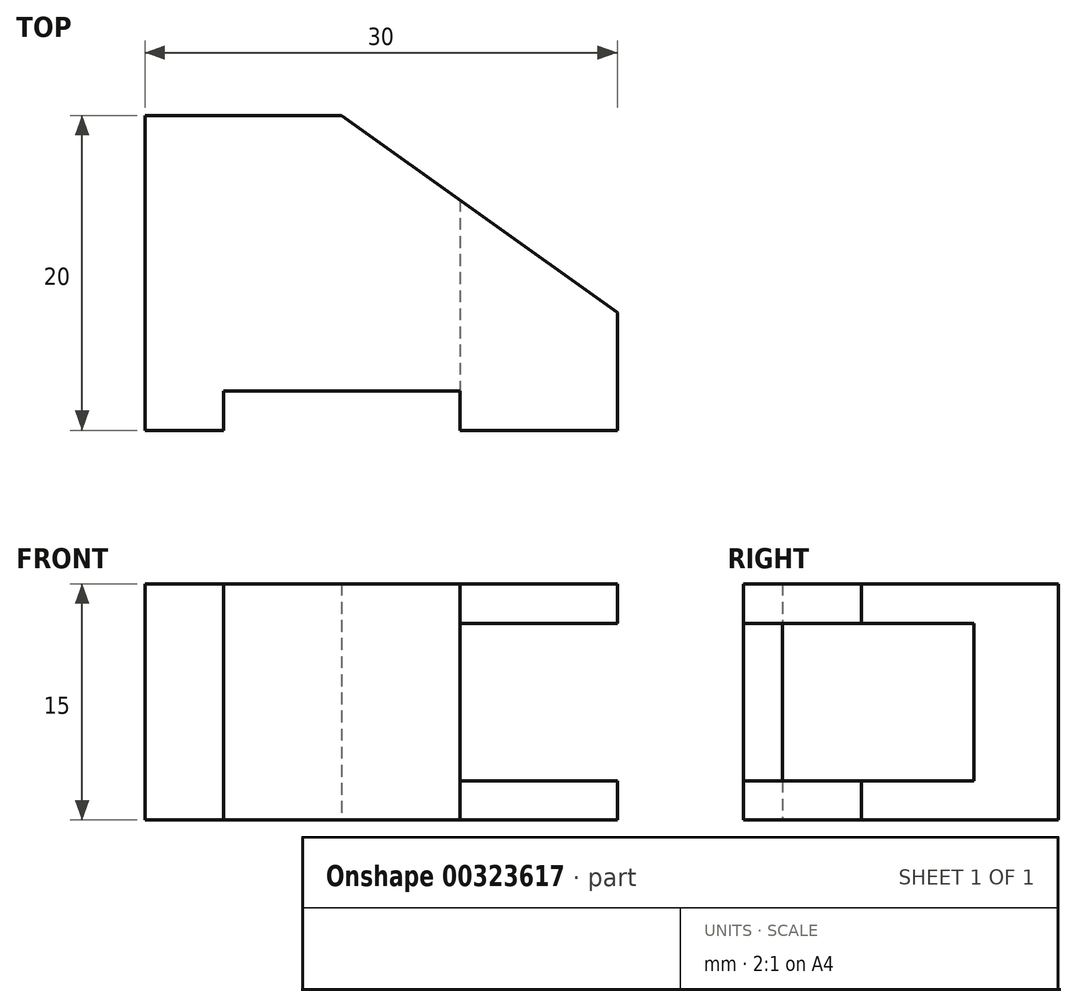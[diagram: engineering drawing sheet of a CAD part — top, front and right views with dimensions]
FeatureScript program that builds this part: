
annotation { "Feature Type Name" : "Feature", "Feature Type Description" : "" }
export const myFeature = defineFeature(function(context is Context, id is Id, definition is map)
    precondition{}
    {
        {
            var Q0;
            Q0=qCreatedBy(makeId("Top.planeOp"),FACE);
            var sketch = newSketch(context, id + "F0", { "sketchPlane" : qUnion([Q0])});
            skLineSegment(sketch, "E0", {"start": v(0, 0) * mm, "end": v(0, 20) * mm});
            skLineSegment(sketch, "E1", {"start": v(0, 20) * mm, "end": v(12.5, 20) * mm});
            skLineSegment(sketch, "E2", {"start": v(12.5, 20) * mm, "end": v(30, 7.5) * mm});
            skLineSegment(sketch, "E3", {"start": v(30, 7.5) * mm, "end": v(30, 0) * mm});
            skLineSegment(sketch, "E4", {"start": v(30, 0) * mm, "end": v(20, 0) * mm});
            skLineSegment(sketch, "E5", {"start": v(20, 0) * mm, "end": v(20, 2.5) * mm});
            skLineSegment(sketch, "E6", {"start": v(20, 2.5) * mm, "end": v(5, 2.5) * mm});
            skLineSegment(sketch, "E7", {"start": v(5, 2.5) * mm, "end": v(5, 0) * mm});
            skLineSegment(sketch, "E8", {"start": v(5, 0) * mm, "end": v(0, 0) * mm});
            skSolve(sketch);
        }
        {
            var Q0;
            Q0=qSketchRegion(id+"F0",true);
            extrude(context, id + "F1", {"entities" : qUnion([Q0]), "depth" : 2.5 * mm});
        }
        {
            var Q0;
            Q0=makeQuery(id+"F1.opExtrude","CAP_FACE",FACE,{"disambiguationData":[OSD([sQuery(id+"F0.wireOp",EDGE,"E0"),sQuery(id+"F0.wireOp",EDGE,"E1"),sQuery(id+"F0.wireOp",EDGE,"E2"),sQuery(id+"F0.wireOp",EDGE,"E3"),sQuery(id+"F0.wireOp",EDGE,"E4"),sQuery(id+"F0.wireOp",EDGE,"E5"),sQuery(id+"F0.wireOp",EDGE,"E6"),sQuery(id+"F0.wireOp",EDGE,"E7"),sQuery(id+"F0.wireOp",EDGE,"E8")])],"isStart":false});
            var sketch = newSketch(context, id + "F2", { "sketchPlane" : qUnion([Q0])});
            skLineSegment(sketch, "E9", {"start": v(0, 0) * mm, "end": v(0, 20) * mm});
            skLineSegment(sketch, "E10", {"start": v(0, 20) * mm, "end": v(12.5, 20) * mm});
            skLineSegment(sketch, "E11", {"start": v(12.5, 20) * mm, "end": v(20, 14.64) * mm});
            skLineSegment(sketch, "E12", {"start": v(20, 14.64) * mm, "end": v(20, 0) * mm});
            skLineSegment(sketch, "E13", {"start": v(20, 0) * mm, "end": v(20, 2.5) * mm});
            skLineSegment(sketch, "E14", {"start": v(20, 2.5) * mm, "end": v(5, 2.5) * mm});
            skLineSegment(sketch, "E15", {"start": v(5, 2.5) * mm, "end": v(5, 0) * mm});
            skLineSegment(sketch, "E16", {"start": v(5, 0) * mm, "end": v(0, 0) * mm});
            skSolve(sketch);
        }
        {
            var Q0;
            Q0=qSketchRegion(id+"F2",true);
            extrude(context, id + "F3", {"entities" : qUnion([Q0]), "operationType" : NewBodyOperationType.ADD, "depth" : 10 * mm});
        }
        {
            var Q0;
            Q0=makeQuery(id+"F3.opExtrude","CAP_FACE",FACE,{"disambiguationData":[OSD([sQuery(id+"F2.wireOp",EDGE,"E9"),sQuery(id+"F2.wireOp",EDGE,"E10"),sQuery(id+"F2.wireOp",EDGE,"E11"),sQuery(id+"F2.wireOp",EDGE,"E12"),sQuery(id+"F2.wireOp",EDGE,"E14"),sQuery(id+"F2.wireOp",EDGE,"E15"),sQuery(id+"F2.wireOp",EDGE,"E16")])],"isStart":false});
            var sketch = newSketch(context, id + "F4", { "sketchPlane" : qUnion([Q0])});
            skLineSegment(sketch, "E17", {"start": v(0, 0) * mm, "end": v(0, 20) * mm});
            skLineSegment(sketch, "E18", {"start": v(0, 20) * mm, "end": v(12.5, 20) * mm});
            skLineSegment(sketch, "E19", {"start": v(12.5, 20) * mm, "end": v(30, 7.5) * mm});
            skLineSegment(sketch, "E20", {"start": v(30, 7.5) * mm, "end": v(30, 0) * mm});
            skLineSegment(sketch, "E21", {"start": v(30, 0) * mm, "end": v(20, 0) * mm});
            skLineSegment(sketch, "E22", {"start": v(20, 0) * mm, "end": v(20, 2.5) * mm});
            skLineSegment(sketch, "E23", {"start": v(20, 2.5) * mm, "end": v(5, 2.5) * mm});
            skLineSegment(sketch, "E24", {"start": v(5, 2.5) * mm, "end": v(5, 0) * mm});
            skLineSegment(sketch, "E25", {"start": v(5, 0) * mm, "end": v(0, 0) * mm});
            skSolve(sketch);
        }
        {
            var Q0;
            Q0=qSketchRegion(id+"F4",true);
            extrude(context, id + "F5", {"entities" : qUnion([Q0]), "operationType" : NewBodyOperationType.ADD, "depth" : 2.5 * mm});
        }
    });
